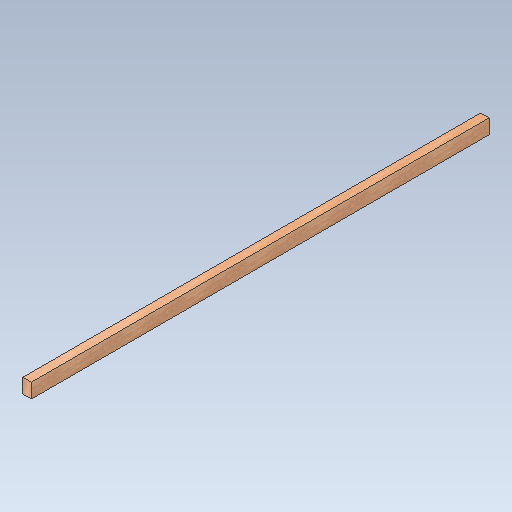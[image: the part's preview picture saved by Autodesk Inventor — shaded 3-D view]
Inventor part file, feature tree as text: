
AUTODESK INVENTOR PART (.ipt)
format: ipt  version: 2020.1 (Build 241239000, 239)  size: 108,032 bytes
history: native  units: mm
features: extrude x1, sketch x1
ambient origin geometry x8: Origin, YZ Plane, XZ Plane, XY Plane, X Axis, Y Axis, Z Axis, Center Point
bodies: Solid1 (feature_tree)
feature tree (2):
  extrude  "Extrusion1"  Depth=60.0mm
  sketch  "Sketch1"  dims[d0=35.0mm d1=60.0mm d2=1884.0mm d3=0.0mm]
